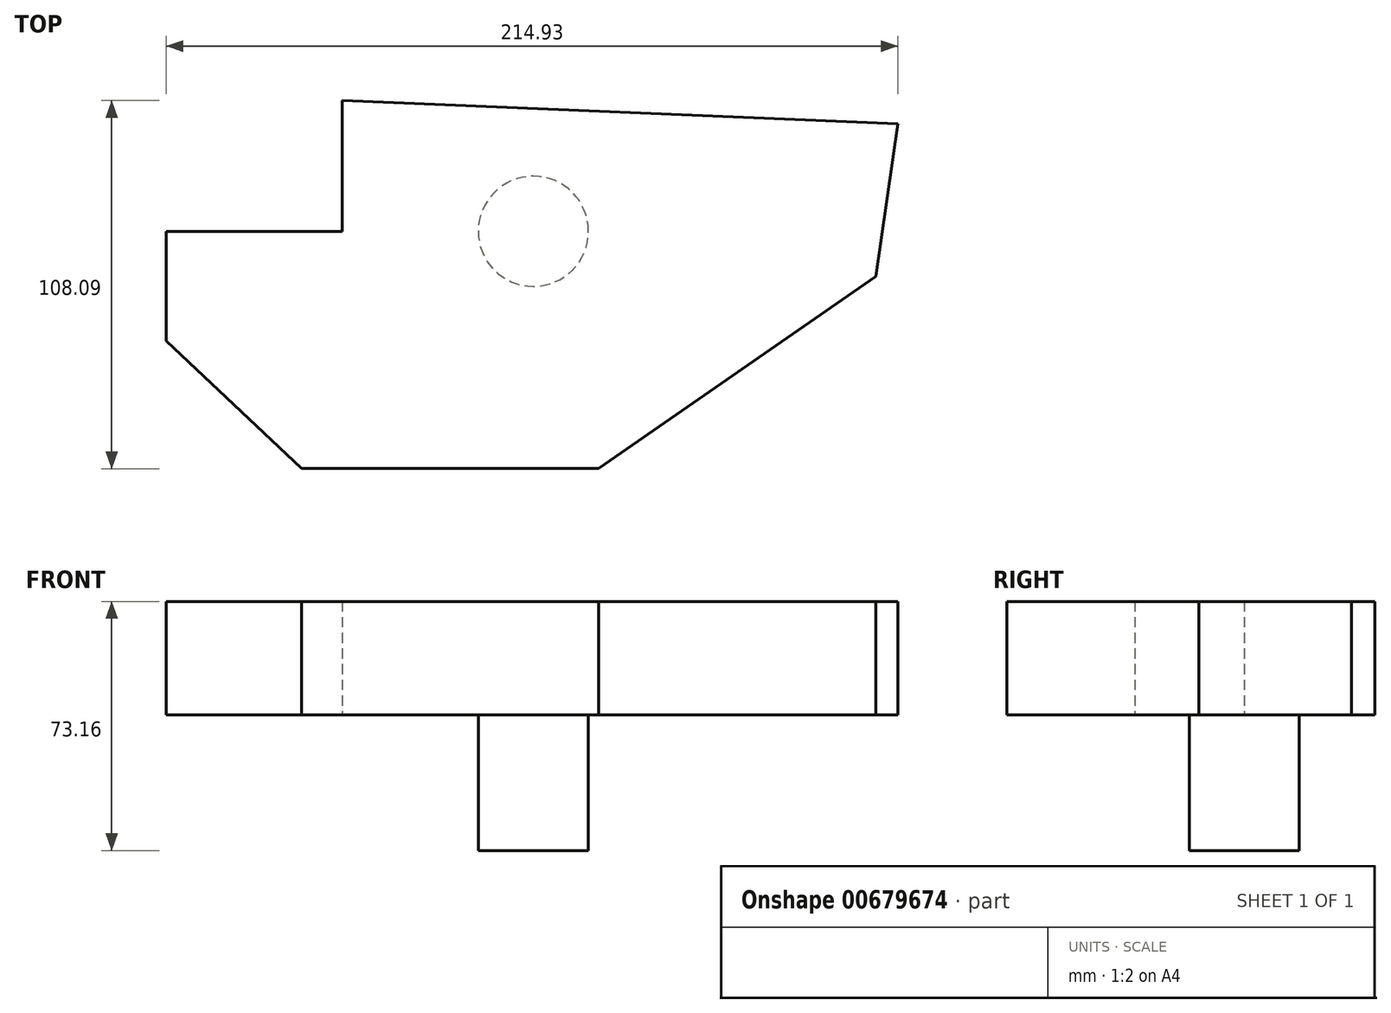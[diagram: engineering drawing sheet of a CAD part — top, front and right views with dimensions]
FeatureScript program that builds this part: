
annotation { "Feature Type Name" : "Feature", "Feature Type Description" : "" }
export const myFeature = defineFeature(function(context is Context, id is Id, definition is map)
    precondition{}
    {
        {
            var Q0;
            Q0=qCreatedBy(makeId("Top.planeOp"),FACE);
            var sketch = newSketch(context, id + "F0", { "sketchPlane" : qUnion([Q0])});
            skLineSegment(sketch, "E0", {"start": v(156.84, -13.28) * mm, "end": v(75.3, -69.7) * mm});
            skLineSegment(sketch, "E1", {"start": v(75.3, -69.7) * mm, "end": v(-11.83, -69.7) * mm});
            skLineSegment(sketch, "E2", {"start": v(-11.83, -69.7) * mm, "end": v(-51.66, -32.16) * mm});
            skLineSegment(sketch, "E3", {"start": v(-51.66, -32.16) * mm, "end": v(-51.66, 0) * mm});
            skLineSegment(sketch, "E4", {"start": v(-51.66, 0) * mm, "end": v(0, 0) * mm});
            skLineSegment(sketch, "E5", {"start": v(0, 0) * mm, "end": v(0, 38.38) * mm});
            skLineSegment(sketch, "E6", {"start": v(0, 38.38) * mm, "end": v(163.27, 31.53) * mm});
            skLineSegment(sketch, "E7", {"start": v(163.27, 31.53) * mm, "end": v(156.84, -13.28) * mm});
            skLineSegment(sketch, "E8", {"start": v(160.05, 9.13) * mm, "end": v(188.37, -17.01) * mm});
            skLineSegment(sketch, "E9", {"start": v(188.37, -17.01) * mm, "end": v(161.4, -43.57) * mm});
            skLineSegment(sketch, "E10", {"start": v(161.4, -43.57) * mm, "end": v(192.52, -56.22) * mm});
            skSolve(sketch);
        }
        {
            var Q0;
            {var subQ0=sQuery(id+"F0.wireOp",EDGE,"E0");Q0=makeQuery(id+"F0.imprint","IMPRINT",FACE,{"disambiguationData":[TD([[makeQuery(id+"F0.imprint","IMPRINT",EDGE,{"derivedFrom":subQ0}),-1.0]])]});}
            var Q1;
            Q1 = qSketchRegion(id + "FpH3ALoUsCjuqET_0", true);
            extrude(context, id + "F1", {"entities" : qUnion([Q0, Q1]), "depth" : 33.35 * mm, "offsetDistance" : 25.4 * mm});
        }
        {
            var Q0;
            Q0=qCreatedBy(makeId("Top.planeOp"),FACE);
            var sketch = newSketch(context, id + "F2", { "sketchPlane" : qUnion([Q0])});
            skCircle(sketch, "E11", {"center": v(56.2, 0) * mm, "radius": 16.18 * mm});
            skSolve(sketch);
        }
        {
            var Q0;
            Q0 = qSketchRegion(id + "F2", true);
            extrude(context, id + "F3", {"entities" : qUnion([Q0]), "operationType" : NewBodyOperationType.ADD, "oppositeDirection" : true, "depth" : 39.81 * mm, "offsetDistance" : 25.4 * mm});
        }
    });
